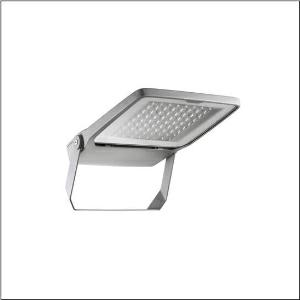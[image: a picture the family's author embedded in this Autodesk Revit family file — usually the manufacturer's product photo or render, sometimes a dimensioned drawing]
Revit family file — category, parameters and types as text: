
# Revit family: floodlight_fl_20_mini___pl52_5xa7671c2d1ac_f48d
name_source: partatom
category: Lighting Fixtures
units: mm (PartAtom-declared; Revit-internal decimal feet)

## family parameters
Cut with Voids When Loaded = No
Host = Face
Light Source = No
Part Type = Normal
Room Calculation Point = No
Round Connector Dimension = Use Diameter
Shared = No

## types (1)
- Floodlight FL 20 mini  PL52 (1 x LED 4000K / CRI = 70 (unbekannt), 12290 lm, 4000K)
    Apparent Load = 96 VA
    CIE Flux Codes = 27 59 98 100 100
    Color Rendering = 70
    Color Temperature = 4000K
    Default Elevation = 1800 mm
    Description = Floodlight FL 20 mini, floodlight, primary light control with lens, of plastic, primary optical cover: protective disc, of toughened safety glass, transparent, light distribution: PL52, light emission: direct distribution, primary light characteristic: asymmetric, installation type: surface-mounted, LED, High Power LED, rated luminous flux: 12.290lm, luminous efficacy: 128lm/W, light colour: 740, colour temperature: 4000K, control gear: ECG Basic, control: power reduction, overheat protection, electronic power reduction, with terminal, 5-pole, max. 2.5mm², mains connection: 220..240V, AC, 50/60Hz, rated input power: 96W, LED unit, of diecast aluminium, powder-coated, Siteco® metallic grey (DB 702S), corrosivity category C5 mid according to DIN EN ISO 12944, incl. 1x M20 cable gland for cable Ø 6.5..12mm, length: 446mm, width: 355mm, height: 62mm, housing frame, of diecast aluminium, powder-coated, Siteco® metallic grey (DB 702S), mounting bracket, of steel, powder-coated, Siteco® metallic grey (DB 702S), ON/OFF, protection rating (complete): IP66, insulation class (complete): insulation class I (protective earthing), certification: CE, ENEC, VDE, protection symbol: D, permissible operating ambient temperature: -40..+40°C, permissible operating ambient temperature for outdoor applications: -40..+50°C, standard: DIN EN 12944, packaging unit: 1 piece

Light Distribution: PL52
    Height = 62 mm  [stored 0.203412 ft]
    Lamp = 1 x LED 4000K / CRI >= 70 (unbekannt)
    Lamp Light Flux = 12290 lm
    Lamp count = 1
    Length = 467 mm
    Luminous efficacy = 128 lm/W
    Manufacturer = Siteco
    ModVariant = No
    Model = 5XA7671C2D1AC
    Mounting Place = Wall
    Mounting Type = Surface mounted
    Number of Poles = 1
    OnlyDefault = Yes
    Power Factor = 1
    Product Name = Floodlight FL 20 mini | PL52
    Product group = floodlight | wall mounted
    ProductGroupID = 2001
    Protection Class = Protection class I
    Protection Degree = IP 66
    RLX_Detail_Level = 1
    RLX_Emergency_Light_Flux = 0 lm
    RLX_Emergency_Type = 0
    RLX_Emergency_Type_DB = No
    RlxData = <blob elided: 70993 chars, md5=00194cd3>
    Socket = socket
    Standby Power = 0 W
    System Light Flux = 12290 lm
    System Power = 96 W
    Type Comments = Product without accessories
    Type Image = l_1005948.jpg
    URL = http://relux.com
    VarID = ---
    Voltage = 0 V
    Weight = 0.00 kg
    Width = 335 mm

note: [stored X ft] marks values corroborated as IEEE doubles in the binary element streams (Revit-internal decimal feet)

## geometry (parser evidence)
native form markers: Blend x4, Sweep x13
no freeform markers — native parametric forms only
